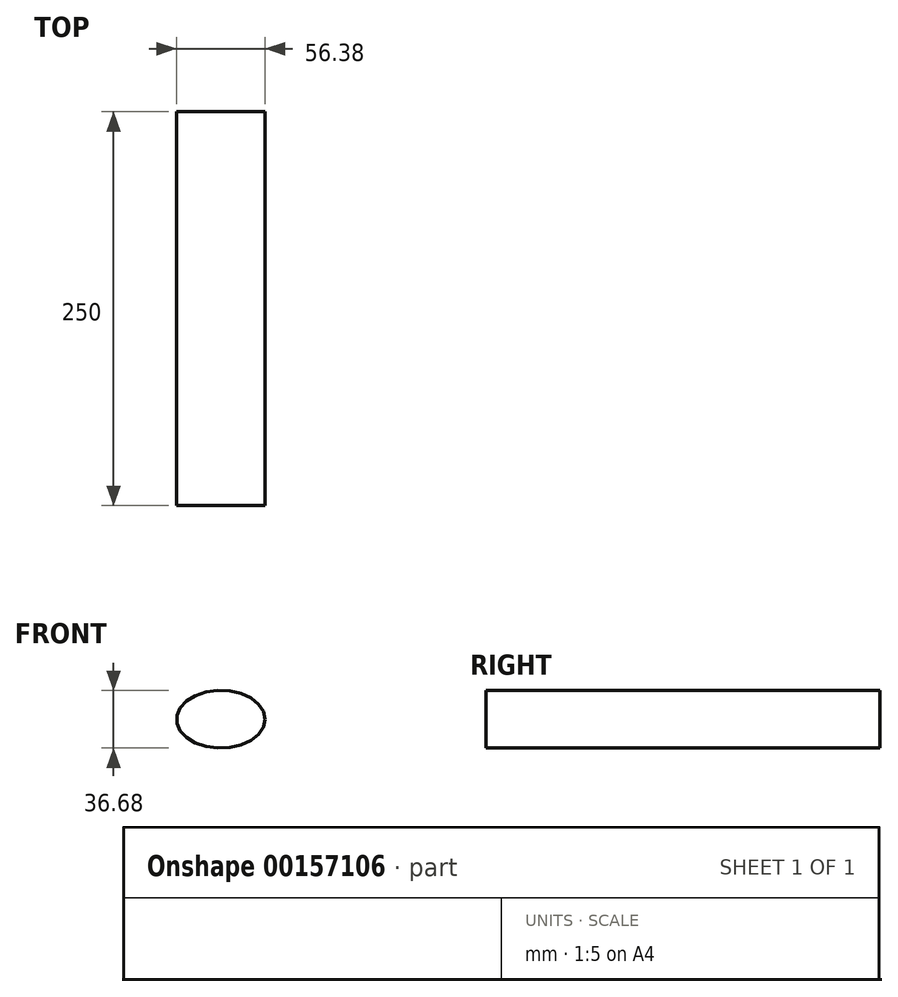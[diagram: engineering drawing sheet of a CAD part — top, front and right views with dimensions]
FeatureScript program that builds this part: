
annotation { "Feature Type Name" : "Feature", "Feature Type Description" : "" }
export const myFeature = defineFeature(function(context is Context, id is Id, definition is map)
    precondition{}
    {
        {
            var Q0;
            Q0=qCreatedBy(makeId("Front.planeOp"),FACE);
            var sketch = newSketch(context, id + "F0", { "sketchPlane" : qUnion([Q0])});
            skEllipse(sketch, "E0", {"center": v(0, 0) * mm, "majorRadius": 28.2 * mm, "minorRadius": 18.34 * mm, "majorAxis": v(1, 0)});
            skSolve(sketch);
        }
        {
            var Q0;
            Q0 = qSketchRegion(id + "F0", true);
            extrude(context, id + "F1", {"entities" : qUnion([Q0]), "depth" : 250 * mm});
        }
    });
